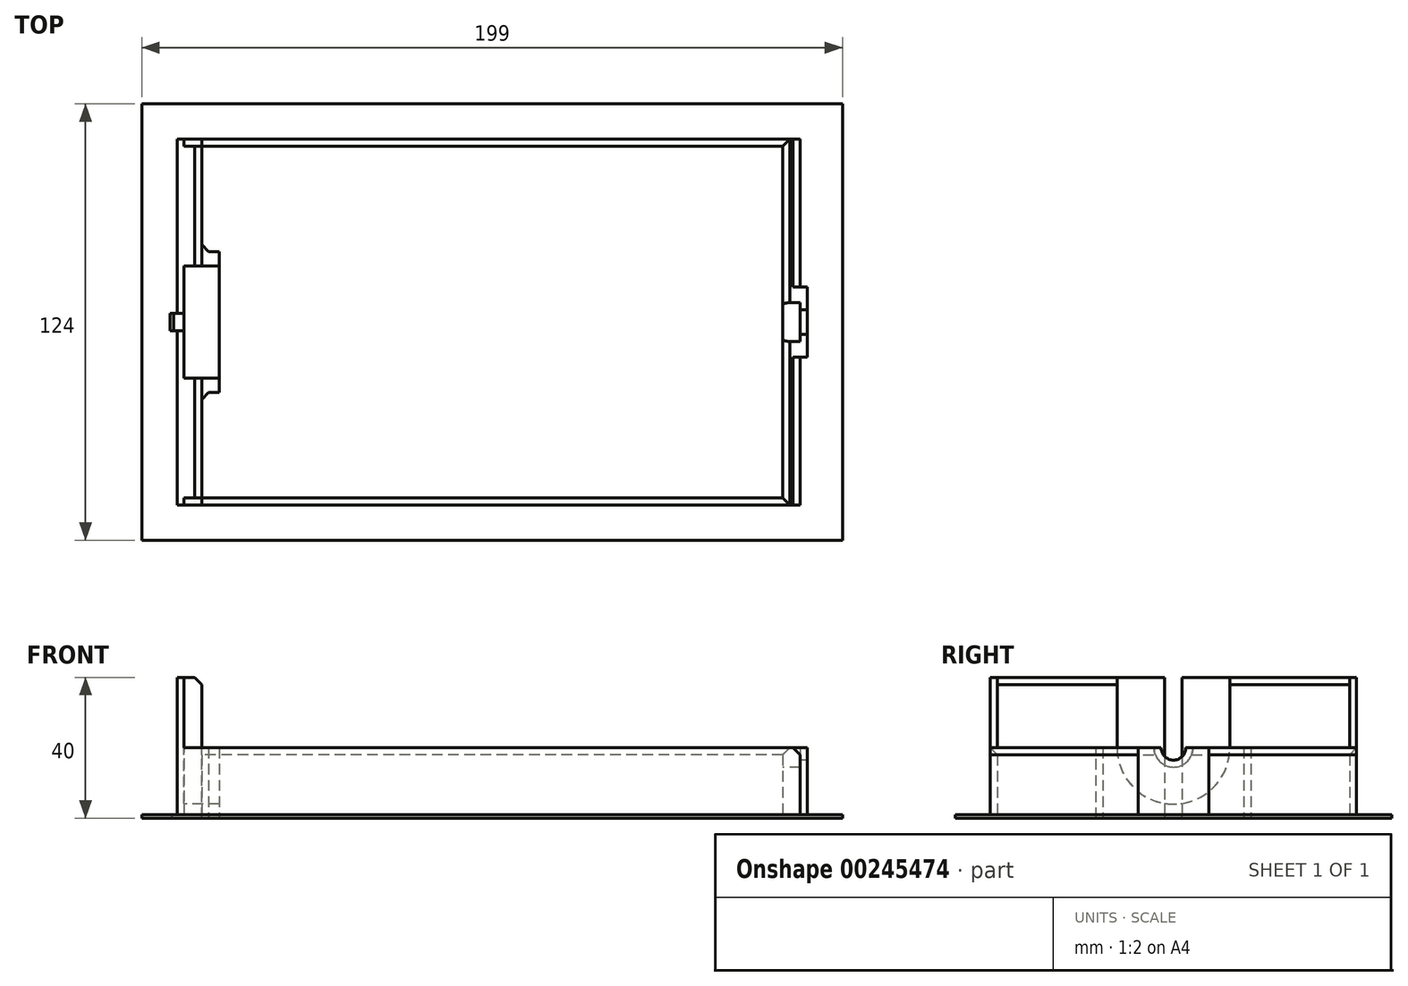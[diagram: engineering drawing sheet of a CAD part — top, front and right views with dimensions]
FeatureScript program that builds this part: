
annotation { "Feature Type Name" : "Feature", "Feature Type Description" : "" }
export const myFeature = defineFeature(function(context is Context, id is Id, definition is map)
    precondition{}
    {
        {
            var Q0;
            Q0=qCreatedBy(makeId("Top.planeOp"),FACE);
            var sketch = newSketch(context, id + "F0", { "sketchPlane" : qUnion([Q0])});
            skLineSegment(sketch, "E0.bottom", {"start": v(-82.5, 50) * mm, "end": v(82.5, 50) * mm});
            skLineSegment(sketch, "E0.top", {"start": v(-82.5, -50) * mm, "end": v(82.5, -50) * mm});
            skLineSegment(sketch, "E0.left", {"start": v(-82.5, 50) * mm, "end": v(-82.5, -50) * mm});
            skLineSegment(sketch, "E0.right", {"start": v(82.5, 50) * mm, "end": v(82.5, -50) * mm});
            skPoint(sketch, "E0.middle", {"position": v(0, 0) * mm});
            skLineSegment(sketch, "E1.bottom", {"start": v(-87.5, 52) * mm, "end": v(87.5, 52) * mm});
            skLineSegment(sketch, "E1.top", {"start": v(-87.5, -52) * mm, "end": v(87.5, -52) * mm});
            skLineSegment(sketch, "E1.left", {"start": v(-87.5, 52) * mm, "end": v(-87.5, -52) * mm});
            skLineSegment(sketch, "E1.right", {"start": v(87.5, 52) * mm, "end": v(87.5, -52) * mm});
            skLineSegment(sketch, "E2.bottom", {"start": v(-89.5, 52) * mm, "end": v(-87.5, 52) * mm});
            skLineSegment(sketch, "E2.top", {"start": v(-89.5, -52) * mm, "end": v(-87.5, -52) * mm});
            skLineSegment(sketch, "E2.left", {"start": v(-89.5, 52) * mm, "end": v(-89.5, -52) * mm});
            skLineSegment(sketch, "E3.bottom", {"start": v(-87.5, 2.5) * mm, "end": v(-89.5, 2.5) * mm});
            skLineSegment(sketch, "E3.top", {"start": v(-87.5, -2.5) * mm, "end": v(-89.5, -2.5) * mm});
            skLineSegment(sketch, "E3.left", {"start": v(-87.5, 2.5) * mm, "end": v(-87.5, -2.5) * mm});
            skLineSegment(sketch, "E3.right", {"start": v(-89.5, 2.5) * mm, "end": v(-89.5, -2.5) * mm});
            skPoint(sketch, "E3.middle", {"position": v(-88.5, 0) * mm});
            skLineSegment(sketch, "E4.bottom", {"start": v(-82.5, 20) * mm, "end": v(-77.5, 20) * mm});
            skLineSegment(sketch, "E4.top", {"start": v(-82.5, -20) * mm, "end": v(-77.5, -20) * mm});
            skLineSegment(sketch, "E4.left", {"start": v(-82.5, 20) * mm, "end": v(-82.5, -20) * mm});
            skLineSegment(sketch, "E4.right", {"start": v(-77.5, 20) * mm, "end": v(-77.5, -20) * mm});
            skPoint(sketch, "E5", {"position": v(-77.5, 0) * mm});
            skLineSegment(sketch, "E6.bottom", {"start": v(87.5, -10) * mm, "end": v(89.5, -10) * mm});
            skLineSegment(sketch, "E6.top", {"start": v(87.5, 10) * mm, "end": v(89.5, 10) * mm});
            skLineSegment(sketch, "E6.left", {"start": v(87.5, -10) * mm, "end": v(87.5, 10) * mm});
            skLineSegment(sketch, "E6.right", {"start": v(89.5, -10) * mm, "end": v(89.5, 10) * mm});
            skPoint(sketch, "E7", {"position": v(89.5, 0) * mm});
            skLineSegment(sketch, "E8.bottom", {"start": v(-99.5, 62) * mm, "end": v(99.5, 62) * mm});
            skLineSegment(sketch, "E8.top", {"start": v(-99.5, -62) * mm, "end": v(99.5, -62) * mm});
            skLineSegment(sketch, "E8.left", {"start": v(-99.5, 62) * mm, "end": v(-99.5, -62) * mm});
            skLineSegment(sketch, "E8.right", {"start": v(99.5, 62) * mm, "end": v(99.5, -62) * mm});
            skSolve(sketch);
        }
        {
            var Q0;
            Q0=makeQuery(id+"F0.imprint","IMPRINT",FACE,{"disambiguationData":[TD([[makeQuery(id+"F0.imprint","IMPRINT",EDGE,{"derivedFrom":sQuery(id+"F0.wireOp",EDGE,"E0.bottom")}),1.0]])]});
            var Q1;
            Q1=makeQuery(id+"F0.imprint","IMPRINT",FACE,{"disambiguationData":[TD([[makeQuery(id+"F0.imprint","IMPRINT",EDGE,{"derivedFrom":sQuery(id+"F0.wireOp",EDGE,"E4.bottom")}),-1.0]])]});
            var Q2;
            Q2=makeQuery(id+"F0.imprint","IMPRINT",FACE,{"disambiguationData":[TD([[makeQuery(id+"F0.imprint","IMPRINT",EDGE,{"derivedFrom":sQuery(id+"F0.wireOp",EDGE,"E6.bottom")}),1.0]])]});
            extrude(context, id + "F1", {"entities" : qUnion([Q0, Q1, Q2]), "depth" : 20 * mm});
        }
        {
            var Q0;
            Q0=makeQuery(id+"F1.opExtrude","SWEPT_FACE",FACE,{"disambiguationData":[OSD([sQuery(id+"F0.wireOp",EDGE,"E1.left")])]});
            var sketch = newSketch(context, id + "F2", { "sketchPlane" : qUnion([Q0])});
            skCircle(sketch, "E9", {"center": v(0, 20) * mm, "radius": 16 * mm});
            skCircle(sketch, "E10", {"center": v(0, 20) * mm, "radius": 5.5 * mm});
            skCircle(sketch, "E11", {"center": v(0, 20) * mm, "radius": 3.5 * mm});
            skSolve(sketch);
        }
        {
            var Q0;
            {var subQ0=sQuery(id+"F2.wireOp",EDGE,"E9");var subQ1=makeQuery(id+"F1.opExtrude","CAP_EDGE",EDGE,{"disambiguationData":[OSD([sQuery(id+"F0.wireOp",EDGE,"E1.left")])],"isStart":false});var subQ2=makeQuery(id+"F2.imprint","INTERSECT",VERTEX,{"disambiguationData":[OD(0.0)],"derivedFrom":[subQ1,subQ0]});Q0=makeQuery(id+"F2.imprint","IMPRINT",FACE,{"disambiguationData":[TD([[makeQuery(id+"F2.imprint","IMPRINT",EDGE,{"disambiguationData":[TD([[subQ2,-1.0]])],"derivedFrom":subQ0}),1.0]])]});}
            var Q1;
            {var subQ0=sQuery(id+"F2.wireOp",EDGE,"E10");var subQ1=makeQuery(id+"F1.opExtrude","CAP_EDGE",EDGE,{"disambiguationData":[OSD([sQuery(id+"F0.wireOp",EDGE,"E1.left")])],"isStart":false});var subQ2=makeQuery(id+"F2.imprint","INTERSECT",VERTEX,{"disambiguationData":[OD(0.0)],"derivedFrom":[subQ1,subQ0]});Q1=makeQuery(id+"F2.imprint","IMPRINT",FACE,{"disambiguationData":[TD([[makeQuery(id+"F2.imprint","IMPRINT",EDGE,{"disambiguationData":[TD([[subQ2,-1.0]])],"derivedFrom":subQ0}),1.0]])]});}
            extrude(context, id + "F3", {"entities" : qUnion([Q0, Q1]), "operationType" : NewBodyOperationType.REMOVE, "endBound" : BoundingType.UP_TO_NEXT, "oppositeDirection" : true, "depth" : 25 * mm});
        }
        {
            var Q0;
            {var subQ0=sQuery(id+"F2.wireOp",EDGE,"E10");var subQ1=makeQuery(id+"F1.opExtrude","CAP_EDGE",EDGE,{"disambiguationData":[OSD([sQuery(id+"F0.wireOp",EDGE,"E1.left")])],"isStart":false});var subQ2=makeQuery(id+"F2.imprint","INTERSECT",VERTEX,{"disambiguationData":[OD(0.0)],"derivedFrom":[subQ1,subQ0]});Q0=makeQuery(id+"F2.imprint","IMPRINT",FACE,{"disambiguationData":[TD([[makeQuery(id+"F2.imprint","IMPRINT",EDGE,{"disambiguationData":[TD([[subQ2,-1.0]])],"derivedFrom":subQ0}),1.0]])]});}
            var Q1;
            {var subQ0=sQuery(id+"F2.wireOp",EDGE,"E11");var subQ1=makeQuery(id+"F1.opExtrude","CAP_EDGE",EDGE,{"disambiguationData":[OSD([sQuery(id+"F0.wireOp",EDGE,"E1.left"),sQuery(id+"F0.wireOp",EDGE,"E3.left")])],"isStart":false});var subQ2=makeQuery(id+"F2.imprint","INTERSECT",VERTEX,{"disambiguationData":[OD(0.0)],"derivedFrom":[subQ1,subQ0]});Q1=makeQuery(id+"F2.imprint","IMPRINT",FACE,{"disambiguationData":[TD([[makeQuery(id+"F2.imprint","IMPRINT",EDGE,{"disambiguationData":[TD([[subQ2,-1.0]])],"derivedFrom":subQ0}),1.0]])]});}
            var Q2;
            Q2=makeQuery(id+"F1.opExtrude","SWEPT_FACE",FACE,{"disambiguationData":[OSD([sQuery(id+"F0.wireOp",EDGE,"E1.right")])]});
            extrude(context, id + "F4", {"entities" : qUnion([Q0, Q1]), "operationType" : NewBodyOperationType.REMOVE, "endBound" : BoundingType.UP_TO_SURFACE, "oppositeDirection" : true, "endBoundEntityFace" : qUnion([Q2]), "depth" : 25 * mm});
        }
        {
            var Q0;
            {var subQ0=sQuery(id+"F0.wireOp",EDGE,"E1.bottom");var subQ1=sQuery(id+"F0.wireOp",EDGE,"E0.left");var subQ2=sQuery(id+"F0.wireOp",EDGE,"E0.right");var subQ3=sQuery(id+"F0.wireOp",EDGE,"E0.bottom");var subQ4=sQuery(id+"F0.wireOp",EDGE,"E1.right");var subQ5=sQuery(id+"F0.wireOp",EDGE,"E1.left");Q0=makeQuery(id+"F4.boolean.opBoolean","SPLIT",FACE,{"disambiguationData":[TD([makeQuery(id+"F1.opExtrude","SWEPT_FACE",FACE,{"disambiguationData":[OSD([subQ3])]})])],"derivedFrom":makeQuery(id+"F1.opExtrude","CAP_FACE",FACE,{"disambiguationData":[OSD([subQ3,sQuery(id+"F0.wireOp",EDGE,"E0.top"),subQ1,subQ2,subQ0,sQuery(id+"F0.wireOp",EDGE,"E1.top"),subQ4,subQ5])],"isStart":false})});}
            var sketch = newSketch(context, id + "F5", { "sketchPlane" : qUnion([Q0])});
            skLineSegment(sketch, "E12.bottom", {"start": v(-82.5, 50) * mm, "end": v(-87.5, 50) * mm});
            skLineSegment(sketch, "E12.top", {"start": v(-82.5, -50) * mm, "end": v(-87.5, -50) * mm});
            skLineSegment(sketch, "E12.left", {"start": v(-82.5, 50) * mm, "end": v(-82.5, -50) * mm});
            skLineSegment(sketch, "E12.right", {"start": v(-87.5, 50) * mm, "end": v(-87.5, -50) * mm});
            skLineSegment(sketch, "E13", {"start": v(-77.5, 16) * mm, "end": v(-87.5, 16) * mm});
            skLineSegment(sketch, "E14.0", {"start": v(-77.5, -16) * mm, "end": v(-87.5, -16) * mm});
            skSolve(sketch);
        }
        {
            var Q0;
            {var subQ0=sQuery(id+"F5.wireOp",EDGE,"E12.bottom");Q0=makeQuery(id+"F5.imprint","IMPRINT",FACE,{"disambiguationData":[TD([[makeQuery(id+"F5.imprint","IMPRINT",EDGE,{"derivedFrom":subQ0}),1.0]])]});}
            var Q1;
            {var subQ0=sQuery(id+"F5.wireOp",EDGE,"E12.top");Q1=makeQuery(id+"F5.imprint","IMPRINT",FACE,{"disambiguationData":[TD([[makeQuery(id+"F5.imprint","IMPRINT",EDGE,{"derivedFrom":subQ0}),-1.0]])]});}
            extrude(context, id + "F6", {"entities" : qUnion([Q0, Q1]), "operationType" : NewBodyOperationType.ADD, "depth" : 20 * mm});
        }
        {
            var Q0;
            {var subQ0=sQuery(id+"F0.wireOp",EDGE,"E2.bottom");Q0=makeQuery(id+"F0.imprint","IMPRINT",FACE,{"disambiguationData":[TD([[makeQuery(id+"F0.imprint","IMPRINT",EDGE,{"derivedFrom":subQ0}),-1.0]])]});}
            var Q1;
            {var subQ0=sQuery(id+"F0.wireOp",EDGE,"E2.top");Q1=makeQuery(id+"F0.imprint","IMPRINT",FACE,{"disambiguationData":[TD([[makeQuery(id+"F0.imprint","IMPRINT",EDGE,{"derivedFrom":subQ0}),1.0]])]});}
            var Q2;
            Q2=makeQuery(id+"F6.opExtrude","CAP_FACE",FACE,{"disambiguationData":[OSD([sQuery(id+"F5.wireOp",EDGE,"E12.top"),sQuery(id+"F5.wireOp",EDGE,"E12.left"),sQuery(id+"F5.wireOp",EDGE,"E12.right"),sQuery(id+"F5.wireOp",EDGE,"E14.0")])],"isStart":false});
            extrude(context, id + "F7", {"entities" : qUnion([Q0, Q1]), "operationType" : NewBodyOperationType.ADD, "endBound" : BoundingType.UP_TO_SURFACE, "endBoundEntityFace" : qUnion([Q2]), "depth" : 25 * mm});
        }
        {
            var Q0;
            {var subQ0=sQuery(id+"F2.wireOp",EDGE,"E11");var subQ1=makeQuery(id+"F1.opExtrude","CAP_EDGE",EDGE,{"disambiguationData":[OSD([sQuery(id+"F0.wireOp",EDGE,"E1.left"),sQuery(id+"F0.wireOp",EDGE,"E3.left")])],"isStart":false});var subQ2=makeQuery(id+"F2.imprint","INTERSECT",VERTEX,{"disambiguationData":[OD(0.0)],"derivedFrom":[subQ1,subQ0]});Q0=makeQuery(id+"F2.imprint","IMPRINT",FACE,{"disambiguationData":[TD([[makeQuery(id+"F2.imprint","IMPRINT",EDGE,{"disambiguationData":[TD([[subQ2,-1.0]])],"derivedFrom":subQ0}),1.0]])]});}
            var Q1;
            {var subQ0=sQuery(id+"F2.wireOp",EDGE,"E11");var subQ1=makeQuery(id+"F1.opExtrude","CAP_EDGE",EDGE,{"disambiguationData":[OSD([sQuery(id+"F0.wireOp",EDGE,"E1.left"),sQuery(id+"F0.wireOp",EDGE,"E3.left")])],"isStart":false});var subQ2=makeQuery(id+"F2.imprint","INTERSECT",VERTEX,{"disambiguationData":[OD(0.0)],"derivedFrom":[subQ1,subQ0]});Q1=makeQuery(id+"F2.imprint","IMPRINT",FACE,{"disambiguationData":[TD([[makeQuery(id+"F2.imprint","IMPRINT",EDGE,{"disambiguationData":[TD([[subQ2,1.0]])],"derivedFrom":subQ0}),1.0]])]});}
            var Q2;
            Q2=makeQuery(id+"F1.opExtrude","SWEPT_FACE",FACE,{"disambiguationData":[OSD([sQuery(id+"F0.wireOp",EDGE,"E6.right")])]});
            extrude(context, id + "F8", {"entities" : qUnion([Q0, Q1]), "operationType" : NewBodyOperationType.REMOVE, "endBound" : BoundingType.UP_TO_SURFACE, "oppositeDirection" : true, "endBoundEntityFace" : qUnion([Q2]), "depth" : 25 * mm});
        }
        {
            var Q0;
            {var subQ5=sQuery(id+"F0.wireOp",EDGE,"E1.bottom");Q0=makeQuery(id+"F0.imprint","IMPRINT",FACE,{"disambiguationData":[TD([[makeQuery(id+"F0.imprint","IMPRINT",EDGE,{"derivedFrom":subQ5}),1.0]])]});}
            extrude(context, id + "F9", {"entities" : qUnion([Q0]), "operationType" : NewBodyOperationType.ADD, "depth" : 1 * mm});
        }
        {
            var Q0;
            {var subQ0=sQuery(id+"F0.wireOp",EDGE,"E2.left");var subQ1=sQuery(id+"F0.wireOp",EDGE,"E2.top");var subQ2=sQuery(id+"F0.wireOp",EDGE,"E3.right");Q0=makeQuery(id+"F9.boolean.opBoolean","SPLIT",EDGE,{"disambiguationData":[topologyDisambiguationEdgeConnected([makeQuery(id+"F7.opExtrude","SWEPT_FACE",FACE,{"disambiguationData":[OSD([subQ0]),TDD([makeQuery(id+"F0.imprint","IMPRINT",EDGE,{"disambiguationData":[TD([[makeQuery(id+"F0.imprint","INTERSECT",VERTEX,{"derivedFrom":[subQ1,subQ0]}),1.0]])],"derivedFrom":subQ0})])]})])],"derivedFrom":makeQuery(id+"F9.opExtrude","CAP_EDGE",EDGE,{"disambiguationData":[OSD([subQ0,subQ2])],"isStart":false})});}
            var Q1;
            Q1=makeQuery(id+"F9.opExtrude","CAP_EDGE",EDGE,{"disambiguationData":[OSD([sQuery(id+"F0.wireOp",EDGE,"E1.top"),sQuery(id+"F0.wireOp",EDGE,"E2.top")])],"isStart":false});
            var Q2;
            {var subQ0=sQuery(id+"F0.wireOp",EDGE,"E2.left");var subQ1=sQuery(id+"F0.wireOp",EDGE,"E2.bottom");var subQ2=sQuery(id+"F0.wireOp",EDGE,"E3.right");Q2=makeQuery(id+"F9.boolean.opBoolean","SPLIT",EDGE,{"disambiguationData":[topologyDisambiguationEdgeConnected([makeQuery(id+"F7.opExtrude","SWEPT_FACE",FACE,{"disambiguationData":[OSD([subQ0]),TDD([makeQuery(id+"F0.imprint","IMPRINT",EDGE,{"disambiguationData":[TD([[makeQuery(id+"F0.imprint","INTERSECT",VERTEX,{"derivedFrom":[subQ1,subQ0]}),-1.0]])],"derivedFrom":subQ0})])]})])],"derivedFrom":makeQuery(id+"F9.opExtrude","CAP_EDGE",EDGE,{"disambiguationData":[OSD([subQ0,subQ2])],"isStart":false})});}
            var Q3;
            Q3=makeQuery(id+"F9.opExtrude","CAP_EDGE",EDGE,{"disambiguationData":[OSD([sQuery(id+"F0.wireOp",EDGE,"E1.bottom"),sQuery(id+"F0.wireOp",EDGE,"E2.bottom")])],"isStart":false});
            var Q4;
            Q4=makeQuery(id+"F6.opExtrude","SWEPT_EDGE",EDGE,{"disambiguationData":[OSD([sQuery(id+"F0.wireOp",EDGE,"E1.left"),sQuery(id+"F0.wireOp",EDGE,"E3.left"),sQuery(id+"F5.wireOp",EDGE,"E12.bottom"),sQuery(id+"F5.wireOp",EDGE,"E12.right")])]});
            var Q5;
            {var subQ0=sQuery(id+"F0.wireOp",EDGE,"E1.right");Q5=makeQuery(id+"F9.opExtrude","CAP_EDGE",EDGE,{"disambiguationData":[OSD([subQ0]),TDD([makeQuery(id+"F0.imprint","IMPRINT",EDGE,{"disambiguationData":[TD([[makeQuery(id+"F0.imprint","INTERSECT",VERTEX,{"derivedFrom":[sQuery(id+"F0.wireOp",EDGE,"E1.bottom"),subQ0]}),-1.0]])],"derivedFrom":subQ0})])],"isStart":false});}
            var Q6;
            {var subQ0=sQuery(id+"F0.wireOp",EDGE,"E1.right");Q6=makeQuery(id+"F9.opExtrude","CAP_EDGE",EDGE,{"disambiguationData":[OSD([subQ0]),TDD([makeQuery(id+"F0.imprint","IMPRINT",EDGE,{"disambiguationData":[TD([[makeQuery(id+"F0.imprint","INTERSECT",VERTEX,{"derivedFrom":[sQuery(id+"F0.wireOp",EDGE,"E1.top"),subQ0]}),1.0]])],"derivedFrom":subQ0})])],"isStart":false});}
            var Q7;
            Q7=makeQuery(id+"F9.opExtrude","CAP_EDGE",EDGE,{"disambiguationData":[OSD([sQuery(id+"F0.wireOp",EDGE,"E6.right")])],"isStart":false});
            var Q8;
            {var subQ0=sQuery(id+"F0.wireOp",EDGE,"E1.right");Q8=makeQuery(id+"F1.opExtrude","CAP_EDGE",EDGE,{"disambiguationData":[OSD([subQ0]),TDD([makeQuery(id+"F0.imprint","IMPRINT",EDGE,{"disambiguationData":[TD([[makeQuery(id+"F0.imprint","INTERSECT",VERTEX,{"derivedFrom":[sQuery(id+"F0.wireOp",EDGE,"E1.top"),subQ0]}),1.0]])],"derivedFrom":subQ0})])],"isStart":false});}
            var Q9;
            {var subQ0=sQuery(id+"F0.wireOp",EDGE,"E1.right");Q9=makeQuery(id+"F1.opExtrude","CAP_EDGE",EDGE,{"disambiguationData":[OSD([subQ0]),TDD([makeQuery(id+"F0.imprint","IMPRINT",EDGE,{"disambiguationData":[TD([[makeQuery(id+"F0.imprint","INTERSECT",VERTEX,{"derivedFrom":[sQuery(id+"F0.wireOp",EDGE,"E1.bottom"),subQ0]}),-1.0]])],"derivedFrom":subQ0})])],"isStart":false});}
            var Q10;
            {var subQ0=sQuery(id+"F0.wireOp",EDGE,"E0.bottom");var subQ1=sQuery(id+"F0.wireOp",EDGE,"E0.right");Q10=makeQuery(id+"F4.boolean.opBoolean","SPLIT",EDGE,{"disambiguationData":[TD([makeQuery(id+"F1.opExtrude","SWEPT_FACE",FACE,{"disambiguationData":[OSD([subQ0])]})])],"derivedFrom":makeQuery(id+"F1.opExtrude","CAP_EDGE",EDGE,{"disambiguationData":[OSD([subQ1])],"isStart":false})});}
            var Q11;
            {var subQ0=sQuery(id+"F0.wireOp",EDGE,"E0.right");var subQ1=sQuery(id+"F0.wireOp",EDGE,"E0.top");Q11=makeQuery(id+"F4.boolean.opBoolean","SPLIT",EDGE,{"disambiguationData":[TD([makeQuery(id+"F1.opExtrude","SWEPT_FACE",FACE,{"disambiguationData":[OSD([subQ1])]})])],"derivedFrom":makeQuery(id+"F1.opExtrude","CAP_EDGE",EDGE,{"disambiguationData":[OSD([subQ0])],"isStart":false})});}
            var Q12;
            Q12=makeQuery(id+"F1.opExtrude","CAP_EDGE",EDGE,{"disambiguationData":[OSD([sQuery(id+"F0.wireOp",EDGE,"E0.bottom")])],"isStart":false});
            var Q13;
            Q13=makeQuery(id+"F1.opExtrude","CAP_EDGE",EDGE,{"disambiguationData":[OSD([sQuery(id+"F0.wireOp",EDGE,"E0.top")])],"isStart":false});
            var Q14;
            {var subQ0=sQuery(id+"F5.wireOp",EDGE,"E12.left");var subQ1=makeQuery(id+"F5.imprint","INTERSECT",VERTEX,{"derivedFrom":[makeQuery(id+"F1.opExtrude","CAP_EDGE",EDGE,{"disambiguationData":[OSD([sQuery(id+"F0.wireOp",EDGE,"E4.top")])],"isStart":false}),subQ0]});Q14=makeQuery(id+"F6.opExtrude","CAP_EDGE",EDGE,{"disambiguationData":[OSD([subQ0]),TDD([makeQuery(id+"F5.imprint","IMPRINT",EDGE,{"disambiguationData":[TD([[subQ1,1.0]])],"derivedFrom":subQ0}),makeQuery(id+"F5.imprint","IMPRINT",EDGE,{"disambiguationData":[TD([[subQ1,-1.0]])],"derivedFrom":subQ0})])],"isStart":false});}
            var Q15;
            {var subQ0=sQuery(id+"F5.wireOp",EDGE,"E12.left");var subQ1=makeQuery(id+"F5.imprint","INTERSECT",VERTEX,{"derivedFrom":[makeQuery(id+"F1.opExtrude","CAP_EDGE",EDGE,{"disambiguationData":[OSD([sQuery(id+"F0.wireOp",EDGE,"E4.bottom")])],"isStart":false}),subQ0]});Q15=makeQuery(id+"F6.opExtrude","CAP_EDGE",EDGE,{"disambiguationData":[OSD([subQ0]),TDD([makeQuery(id+"F5.imprint","IMPRINT",EDGE,{"disambiguationData":[TD([[subQ1,1.0]])],"derivedFrom":subQ0}),makeQuery(id+"F5.imprint","IMPRINT",EDGE,{"disambiguationData":[TD([[subQ1,-1.0]])],"derivedFrom":subQ0})])],"isStart":false});}
            var Q16;
            {var subQ0=sQuery(id+"F0.wireOp",EDGE,"E2.left");Q16=makeQuery(id+"F7.opExtrude","TWEAK_EDGE",EDGE,{"derivedFrom":[makeQuery(id+"F0.imprint","IMPRINT",EDGE,{"disambiguationData":[TD([[makeQuery(id+"F0.imprint","INTERSECT",VERTEX,{"derivedFrom":[sQuery(id+"F0.wireOp",EDGE,"E2.top"),subQ0]}),1.0]])],"derivedFrom":subQ0}),makeQuery(id+"F6.opExtrude","CAP_FACE",FACE,{"disambiguationData":[OSD([sQuery(id+"F5.wireOp",EDGE,"E12.top"),sQuery(id+"F5.wireOp",EDGE,"E12.left"),sQuery(id+"F5.wireOp",EDGE,"E12.right"),sQuery(id+"F5.wireOp",EDGE,"E14.0")])],"isStart":false})]});}
            var Q17;
            {var subQ0=sQuery(id+"F0.wireOp",EDGE,"E2.left");Q17=makeQuery(id+"F7.opExtrude","TWEAK_EDGE",EDGE,{"derivedFrom":[makeQuery(id+"F0.imprint","IMPRINT",EDGE,{"disambiguationData":[TD([[makeQuery(id+"F0.imprint","INTERSECT",VERTEX,{"derivedFrom":[sQuery(id+"F0.wireOp",EDGE,"E2.bottom"),subQ0]}),-1.0]])],"derivedFrom":subQ0}),makeQuery(id+"F6.opExtrude","CAP_FACE",FACE,{"disambiguationData":[OSD([sQuery(id+"F5.wireOp",EDGE,"E12.top"),sQuery(id+"F5.wireOp",EDGE,"E12.left"),sQuery(id+"F5.wireOp",EDGE,"E12.right"),sQuery(id+"F5.wireOp",EDGE,"E14.0")])],"isStart":false})]});}
            var Q18;
            Q18=makeQuery(id+"F6.opExtrude","SWEPT_EDGE",EDGE,{"disambiguationData":[OSD([sQuery(id+"F0.wireOp",EDGE,"E1.left"),sQuery(id+"F0.wireOp",EDGE,"E3.left"),sQuery(id+"F5.wireOp",EDGE,"E12.top"),sQuery(id+"F5.wireOp",EDGE,"E12.right")])]});
            var Q19;
            Q19=makeQuery(id+"F1.opExtrude","SWEPT_EDGE",EDGE,{"disambiguationData":[OSD([sQuery(id+"F0.wireOp",EDGE,"E0.left"),sQuery(id+"F0.wireOp",EDGE,"E4.top"),sQuery(id+"F0.wireOp",EDGE,"E4.left")])]});
            var Q20;
            Q20=makeQuery(id+"F1.opExtrude","SWEPT_EDGE",EDGE,{"disambiguationData":[OSD([sQuery(id+"F0.wireOp",EDGE,"E0.left"),sQuery(id+"F0.wireOp",EDGE,"E4.bottom"),sQuery(id+"F0.wireOp",EDGE,"E4.left")])]});
            var Q21;
            {var subQ0=sQuery(id+"F2.wireOp",EDGE,"E9");var subQ1=makeQuery(id+"F1.opExtrude","CAP_EDGE",EDGE,{"disambiguationData":[OSD([sQuery(id+"F0.wireOp",EDGE,"E1.left"),sQuery(id+"F0.wireOp",EDGE,"E3.left")])],"isStart":false});Q21=makeQuery(id+"F3.boolean.opBoolean","COPY",EDGE,{"derivedFrom":makeQuery(id+"F3.opExtrude","TWEAK_EDGE",EDGE,{"derivedFrom":[makeQuery(id+"F1.opExtrude","SWEPT_FACE",FACE,{"disambiguationData":[OSD([sQuery(id+"F0.wireOp",EDGE,"E4.right")])]}),makeQuery(id+"F2.imprint","IMPRINT",EDGE,{"disambiguationData":[TD([[makeQuery(id+"F2.imprint","INTERSECT",VERTEX,{"disambiguationData":[OD(0.0)],"derivedFrom":[subQ1,subQ0]}),-1.0]])],"derivedFrom":subQ0})]})});}
            chamfer(context, id + "F10", {"entities" : qUnion([Q0, Q1, Q2, Q3, Q4, Q5, Q6, Q7, Q8, Q9, Q10, Q11, Q12, Q13, Q14, Q15, Q16, Q17, Q18, Q19, Q20, Q21]), "width" : 2 * mm, "tangentPropagation" : true});
        }
    });
